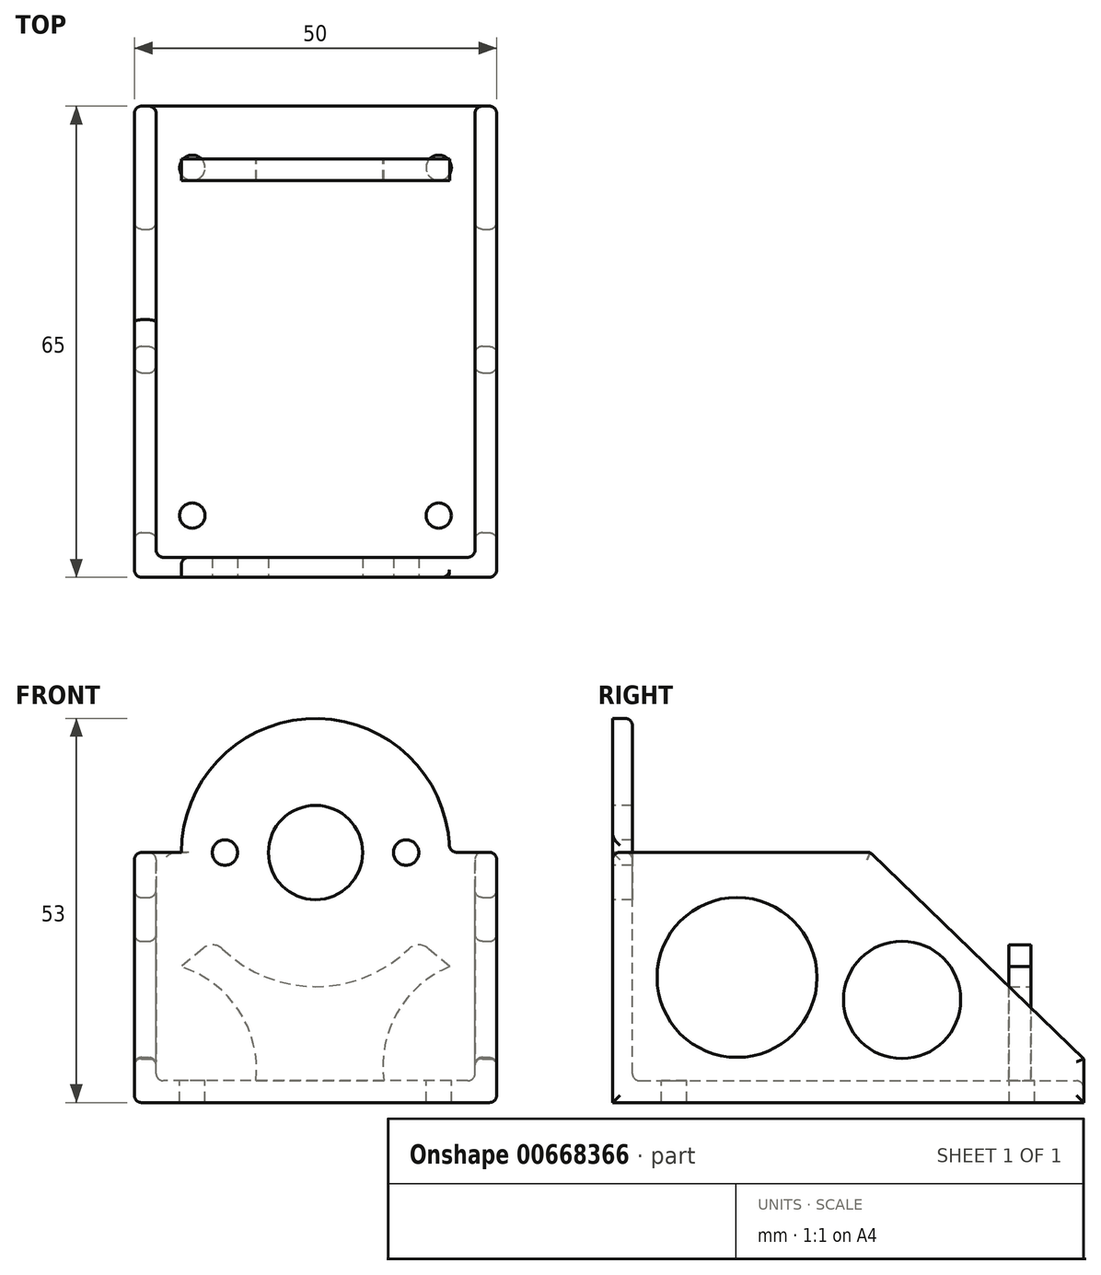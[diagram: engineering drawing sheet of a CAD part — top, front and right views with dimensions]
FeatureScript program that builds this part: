
annotation { "Feature Type Name" : "Feature", "Feature Type Description" : "" }
export const myFeature = defineFeature(function(context is Context, id is Id, definition is map)
    precondition{}
    {
        {
            var Q0;
            Q0=qCreatedBy(makeId("Top.planeOp"),FACE);
            var sketch = newSketch(context, id + "F0", { "sketchPlane" : qUnion([Q0])});
            skLineSegment(sketch, "E0.bottom", {"start": v(25, -32.5) * mm, "end": v(-25, -32.5) * mm});
            skLineSegment(sketch, "E0.top", {"start": v(25, 32.5) * mm, "end": v(-25, 32.5) * mm});
            skLineSegment(sketch, "E0.left", {"start": v(25, -32.5) * mm, "end": v(25, 32.5) * mm});
            skLineSegment(sketch, "E0.right", {"start": v(-25, -32.5) * mm, "end": v(-25, 32.5) * mm});
            skPoint(sketch, "E0.middle", {"position": v(0, 0) * mm});
            skSolve(sketch);
        }
        {
            var Q0;
            Q0 = qSketchRegion(id + "F0", true);
            extrude(context, id + "F1", {"entities" : qUnion([Q0]), "depth" : 53 * mm, "offsetDistance" : 25.4 * mm});
        }
        {
            var Q0;
            Q0=makeQuery(id+"F1.opExtrude","CAP_FACE",FACE,{"disambiguationData":[OSD([sQuery(id+"F0.wireOp",EDGE,"E0.bottom"),sQuery(id+"F0.wireOp",EDGE,"E0.top"),sQuery(id+"F0.wireOp",EDGE,"E0.left"),sQuery(id+"F0.wireOp",EDGE,"E0.right")])],"isStart":false});
            var sketch = newSketch(context, id + "F2", { "sketchPlane" : qUnion([Q0])});
            skLineSegment(sketch, "E1.bottom", {"start": v(22, -29.76) * mm, "end": v(-22, -29.76) * mm});
            skLineSegment(sketch, "E1.top", {"start": v(22, 34.24) * mm, "end": v(-22, 34.24) * mm});
            skLineSegment(sketch, "E1.left", {"start": v(22, -29.76) * mm, "end": v(22, 34.24) * mm});
            skLineSegment(sketch, "E1.right", {"start": v(-22, -29.76) * mm, "end": v(-22, 34.24) * mm});
            skPoint(sketch, "E1.middle", {"position": v(0, 2.24) * mm});
            skSolve(sketch);
        }
        {
            var Q0;
            Q0 = qSketchRegion(id + "F2", true);
            extrude(context, id + "F3", {"entities" : qUnion([Q0]), "operationType" : NewBodyOperationType.REMOVE, "oppositeDirection" : true, "depth" : 50 * mm, "offsetDistance" : 25.4 * mm});
        }
        {
            var Q0;
            Q0=makeQuery(id+"F1.opExtrude","SWEPT_FACE",FACE,{"disambiguationData":[OSD([sQuery(id+"F0.wireOp",EDGE,"E0.left")])]});
            var sketch = newSketch(context, id + "F4", { "sketchPlane" : qUnion([Q0])});
            skLineSegment(sketch, "E2", {"start": v(-16.13, 53) * mm, "end": v(32.5, 6.03) * mm});
            skSolve(sketch);
        }
        {
            var Q0;
            {var subQ0=sQuery(id+"F4.wireOp",EDGE,"E2");Q0=makeQuery(id+"F4.imprint","IMPRINT",FACE,{"disambiguationData":[TD([[makeQuery(id+"F4.imprint","IMPRINT",EDGE,{"derivedFrom":subQ0}),1.0]])]});}
            var Q1;
            Q1=sQuery(id+"F4.wireOp",EDGE,"E2");
            extrude(context, id + "F5", {"entities" : qUnion([Q0]), "operationType" : NewBodyOperationType.REMOVE, "surfaceEntities" : qUnion([Q1]), "oppositeDirection" : true, "depth" : 50.8 * mm, "offsetDistance" : 25.4 * mm});
        }
        {
            var Q0;
            Q0=makeQuery(id+"F1.opExtrude","SWEPT_FACE",FACE,{"disambiguationData":[OSD([sQuery(id+"F0.wireOp",EDGE,"E0.bottom")])]});
            var sketch = newSketch(context, id + "F6", { "sketchPlane" : qUnion([Q0])});
            skLineSegment(sketch, "E3", {"start": v(0, 0) * mm, "end": v(0, 34.5) * mm});
            skCircle(sketch, "E4", {"center": v(0, 34.5) * mm, "radius": 18.5 * mm});
            skLineSegment(sketch, "E5", {"start": v(0, 34.5) * mm, "end": v(12.5, 34.5) * mm});
            skLineSegment(sketch, "E6", {"start": v(12.5, 34.5) * mm, "end": v(0, 34.5) * mm});
            skLineSegment(sketch, "E7", {"start": v(0, 34.5) * mm, "end": v(-12.5, 34.5) * mm});
            skCircle(sketch, "E8", {"center": v(-12.5, 34.5) * mm, "radius": 1.75 * mm});
            skCircle(sketch, "E9", {"center": v(12.5, 34.5) * mm, "radius": 1.75 * mm});
            skCircle(sketch, "E10", {"center": v(0, 34.5) * mm, "radius": 6.5 * mm});
            skLineSegment(sketch, "E11", {"start": v(18.5, 34.53) * mm, "end": v(25, 34.53) * mm});
            skLineSegment(sketch, "E12", {"start": v(-18.5, 34.5) * mm, "end": v(-25, 34.5) * mm});
            skSolve(sketch);
        }
        {
            var Q0;
            Q0=makeQuery(id+"F6.imprint","IMPRINT",FACE,{"disambiguationData":[TD([[makeQuery(id+"F6.imprint","IMPRINT",EDGE,{"derivedFrom":sQuery(id+"F6.wireOp",EDGE,"E8")}),1.0]])]});
            var Q1;
            Q1=makeQuery(id+"F6.imprint","IMPRINT",FACE,{"disambiguationData":[TD([[makeQuery(id+"F6.imprint","IMPRINT",EDGE,{"derivedFrom":sQuery(id+"F6.wireOp",EDGE,"E9")}),1.0]])]});
            var Q2;
            {var subQ1=sQuery(id+"F6.wireOp",EDGE,"E6");var subQ3=sQuery(id+"F6.wireOp",EDGE,"E10");var subQ4=makeQuery(id+"F6.imprint","INTERSECT",VERTEX,{"derivedFrom":[subQ1,subQ3]});Q2=makeQuery(id+"F6.imprint","IMPRINT",FACE,{"disambiguationData":[TD([[makeQuery(id+"F6.imprint","IMPRINT",EDGE,{"disambiguationData":[TD([[subQ4,-1.0]])],"derivedFrom":subQ3}),1.0]])]});}
            var Q3;
            {var subQ1=sQuery(id+"F6.wireOp",EDGE,"E3");var subQ3=sQuery(id+"F6.wireOp",EDGE,"E10");var subQ4=makeQuery(id+"F6.imprint","INTERSECT",VERTEX,{"derivedFrom":[subQ1,subQ3]});Q3=makeQuery(id+"F6.imprint","IMPRINT",FACE,{"disambiguationData":[TD([[makeQuery(id+"F6.imprint","IMPRINT",EDGE,{"disambiguationData":[TD([[subQ4,-1.0]])],"derivedFrom":subQ3}),1.0]])]});}
            var Q4;
            {var subQ1=sQuery(id+"F6.wireOp",EDGE,"E3");var subQ3=sQuery(id+"F6.wireOp",EDGE,"E10");var subQ4=makeQuery(id+"F6.imprint","INTERSECT",VERTEX,{"derivedFrom":[subQ1,subQ3]});Q4=makeQuery(id+"F6.imprint","IMPRINT",FACE,{"disambiguationData":[TD([[makeQuery(id+"F6.imprint","IMPRINT",EDGE,{"disambiguationData":[TD([[subQ4,1.0]])],"derivedFrom":subQ3}),1.0]])]});}
            var Q5;
            {var subQ0=sQuery(id+"F6.wireOp",EDGE,"E12");Q5=makeQuery(id+"F6.imprint","IMPRINT",FACE,{"disambiguationData":[TD([[makeQuery(id+"F6.imprint","IMPRINT",EDGE,{"derivedFrom":subQ0}),-1.0]])]});}
            var Q6;
            {var subQ0=sQuery(id+"F6.wireOp",EDGE,"E11");Q6=makeQuery(id+"F6.imprint","IMPRINT",FACE,{"disambiguationData":[TD([[makeQuery(id+"F6.imprint","IMPRINT",EDGE,{"derivedFrom":subQ0}),1.0]])]});}
            extrude(context, id + "F7", {"entities" : qUnion([Q0, Q1, Q2, Q3, Q4, Q5, Q6]), "operationType" : NewBodyOperationType.REMOVE, "oppositeDirection" : true, "depth" : 46.48 * mm, "offsetDistance" : 25.4 * mm});
        }
        {
            var Q0;
            Q0=makeQuery(id+"F1.opExtrude","SWEPT_FACE",FACE,{"disambiguationData":[OSD([sQuery(id+"F0.wireOp",EDGE,"E0.left")])]});
            var sketch = newSketch(context, id + "F8", { "sketchPlane" : qUnion([Q0])});
            skCircle(sketch, "E13", {"center": v(-15.34, 17.27) * mm, "radius": 11.03 * mm});
            skPoint(sketch, "E13.centerSnap0", {"position": v(-32.5, 17.27) * mm});
            skLineSegment(sketch, "E14", {"start": v(-13.31, 6.42) * mm, "end": v(32.1, 6.42) * mm});
            skCircle(sketch, "E15", {"center": v(7.43, 14.17) * mm, "radius": 8.1 * mm});
            skSolve(sketch);
        }
        {
            var Q0;
            Q0 = qSketchRegion(id + "F8", true);
            extrude(context, id + "F9", {"entities" : qUnion([Q0]), "operationType" : NewBodyOperationType.REMOVE, "oppositeDirection" : true, "depth" : 51.05 * mm, "offsetDistance" : 25.4 * mm});
        }
        {
            var Q0;
            Q0=makeQuery(id+"F1.opExtrude","SWEPT_FACE",FACE,{"disambiguationData":[OSD([sQuery(id+"F0.wireOp",EDGE,"E0.left")])]});
            var Q1;
            Q1=makeQuery(id+"F3.boolean.opBoolean","COPY",FACE,{"derivedFrom":makeQuery(id+"F3.opExtrude","SWEPT_FACE",FACE,{"disambiguationData":[OSD([sQuery(id+"F2.wireOp",EDGE,"E1.right")])]})});
            var Q2;
            Q2=makeQuery(id+"F3.boolean.opBoolean","COPY",FACE,{"derivedFrom":makeQuery(id+"F3.opExtrude","SWEPT_FACE",FACE,{"disambiguationData":[OSD([sQuery(id+"F2.wireOp",EDGE,"E1.left")])]})});
            var Q3;
            Q3=makeQuery(id+"F1.opExtrude","SWEPT_FACE",FACE,{"disambiguationData":[OSD([sQuery(id+"F0.wireOp",EDGE,"E0.right")])]});
            var Q4;
            Q4=makeQuery(id+"F3.boolean.opBoolean","COPY",FACE,{"derivedFrom":makeQuery(id+"F3.opExtrude","CAP_FACE",FACE,{"disambiguationData":[OSD([sQuery(id+"F2.wireOp",EDGE,"E1.bottom"),sQuery(id+"F2.wireOp",EDGE,"E1.top"),sQuery(id+"F2.wireOp",EDGE,"E1.left"),sQuery(id+"F2.wireOp",EDGE,"E1.right")])],"isStart":false})});
            var Q5;
            {var subQ0=sQuery(id+"F6.wireOp",EDGE,"E4");Q5=makeQuery(id+"F7.boolean.opBoolean","INTERSECT",EDGE,{"derivedFrom":[makeQuery(id+"F3.boolean.opBoolean","COPY",FACE,{"derivedFrom":makeQuery(id+"F3.opExtrude","SWEPT_FACE",FACE,{"disambiguationData":[OSD([sQuery(id+"F2.wireOp",EDGE,"E1.bottom")])]})}),makeQuery(id+"F7.opExtrude","SWEPT_FACE",FACE,{"disambiguationData":[OSD([subQ0]),TDD([makeQuery(id+"F6.imprint","IMPRINT",EDGE,{"disambiguationData":[TD([[makeQuery(id+"F6.imprint","INTERSECT",VERTEX,{"derivedFrom":[subQ0,sQuery(id+"F6.wireOp",EDGE,"E11")]}),-1.0]])],"derivedFrom":subQ0})])]}),makeQuery(id+"F7.opExtrude","SWEPT_FACE",FACE,{"disambiguationData":[OSD([subQ0]),TDD([makeQuery(id+"F6.imprint","IMPRINT",EDGE,{"disambiguationData":[TD([[makeQuery(id+"F6.imprint","INTERSECT",VERTEX,{"derivedFrom":[subQ0,sQuery(id+"F6.wireOp",EDGE,"E12")]}),1.0]])],"derivedFrom":subQ0})])]})]});}
            var Q6;
            Q6=makeQuery(id+"F7.boolean.opBoolean","COPY",FACE,{"derivedFrom":makeQuery(id+"F7.opExtrude","SWEPT_FACE",FACE,{"disambiguationData":[OSD([sQuery(id+"F6.wireOp",EDGE,"E11")])]})});
            var Q7;
            {var subQ0=sQuery(id+"F6.wireOp",EDGE,"E4");Q7=makeQuery(id+"F7.boolean.opBoolean","TWEAK_FACE",FACE,{"derivedFrom":[makeQuery(id+"F7.opExtrude","SWEPT_FACE",FACE,{"disambiguationData":[OSD([subQ0]),TDD([makeQuery(id+"F6.imprint","IMPRINT",EDGE,{"disambiguationData":[TD([[makeQuery(id+"F6.imprint","INTERSECT",VERTEX,{"derivedFrom":[subQ0,sQuery(id+"F6.wireOp",EDGE,"E11")]}),-1.0]])],"derivedFrom":subQ0})])]}),makeQuery(id+"F7.opExtrude","SWEPT_FACE",FACE,{"disambiguationData":[OSD([subQ0]),TDD([makeQuery(id+"F6.imprint","IMPRINT",EDGE,{"disambiguationData":[TD([[makeQuery(id+"F6.imprint","INTERSECT",VERTEX,{"derivedFrom":[subQ0,sQuery(id+"F6.wireOp",EDGE,"E12")]}),1.0]])],"derivedFrom":subQ0})])]})]});}
            var Q8;
            Q8=makeQuery(id+"F7.boolean.opBoolean","COPY",EDGE,{"derivedFrom":makeQuery(id+"F7.opExtrude","CAP_EDGE",EDGE,{"disambiguationData":[OSD([sQuery(id+"F6.wireOp",EDGE,"E12")])],"isStart":true})});
            fillet(context, id + "F10", {"entities" : qUnion([Q0, Q1, Q2, Q3, Q4, Q5, Q6, Q7, Q8]), "radius" : 1 * mm, "tangentPropagation" : true, "allowEdgeOverflow" : false});
        }
        {
            var Q0;
            Q0=makeQuery(id+"F3.boolean.opBoolean","COPY",FACE,{"derivedFrom":makeQuery(id+"F3.opExtrude","CAP_FACE",FACE,{"disambiguationData":[OSD([sQuery(id+"F2.wireOp",EDGE,"E1.bottom"),sQuery(id+"F2.wireOp",EDGE,"E1.top"),sQuery(id+"F2.wireOp",EDGE,"E1.left"),sQuery(id+"F2.wireOp",EDGE,"E1.right")])],"isStart":false})});
            var sketch = newSketch(context, id + "F11", { "sketchPlane" : qUnion([Q0])});
            skLineSegment(sketch, "E16.bottom", {"start": v(-17, -24) * mm, "end": v(17, -24) * mm});
            skLineSegment(sketch, "E16.top", {"start": v(-17, 24) * mm, "end": v(17, 24) * mm});
            skLineSegment(sketch, "E16.left", {"start": v(-17, -24) * mm, "end": v(-17, 24) * mm});
            skLineSegment(sketch, "E16.right", {"start": v(17, -24) * mm, "end": v(17, 24) * mm});
            skPoint(sketch, "E16.middle", {"position": v(0, 0) * mm});
            skCircle(sketch, "E17", {"center": v(17, -24) * mm, "radius": 1.75 * mm});
            skCircle(sketch, "E18", {"center": v(-17, -24) * mm, "radius": 1.75 * mm});
            skCircle(sketch, "E19", {"center": v(17, 24) * mm, "radius": 1.75 * mm});
            skCircle(sketch, "E20", {"center": v(-17, 24) * mm, "radius": 1.75 * mm});
            skSolve(sketch);
        }
        {
            var Q0;
            {var subQ0=sQuery(id+"F11.wireOp",EDGE,"E16.left");var subQ1=sQuery(id+"F11.wireOp",EDGE,"E16.top");var subQ2=makeQuery(id+"F11.imprint","INTERSECT",VERTEX,{"derivedFrom":[subQ1,subQ0]});Q0=makeQuery(id+"F11.imprint","IMPRINT",FACE,{"disambiguationData":[TD([[makeQuery(id+"F11.imprint","IMPRINT",EDGE,{"disambiguationData":[TD([[subQ2,-1.0]])],"derivedFrom":subQ1}),1.0]])]});}
            var Q1;
            {var subQ0=sQuery(id+"F11.wireOp",EDGE,"E16.right");var subQ1=sQuery(id+"F11.wireOp",EDGE,"E16.top");var subQ2=makeQuery(id+"F11.imprint","INTERSECT",VERTEX,{"derivedFrom":[subQ1,subQ0]});Q1=makeQuery(id+"F11.imprint","IMPRINT",FACE,{"disambiguationData":[TD([[makeQuery(id+"F11.imprint","IMPRINT",EDGE,{"disambiguationData":[TD([[subQ2,1.0]])],"derivedFrom":subQ1}),1.0]])]});}
            var Q2;
            {var subQ0=sQuery(id+"F11.wireOp",EDGE,"E16.right");var subQ1=sQuery(id+"F11.wireOp",EDGE,"E16.top");var subQ2=makeQuery(id+"F11.imprint","INTERSECT",VERTEX,{"derivedFrom":[subQ1,subQ0]});Q2=makeQuery(id+"F11.imprint","IMPRINT",FACE,{"disambiguationData":[TD([[makeQuery(id+"F11.imprint","IMPRINT",EDGE,{"disambiguationData":[TD([[subQ2,1.0]])],"derivedFrom":subQ1}),-1.0]])]});}
            var Q3;
            {var subQ0=sQuery(id+"F11.wireOp",EDGE,"E16.left");var subQ1=sQuery(id+"F11.wireOp",EDGE,"E16.top");var subQ2=makeQuery(id+"F11.imprint","INTERSECT",VERTEX,{"derivedFrom":[subQ1,subQ0]});Q3=makeQuery(id+"F11.imprint","IMPRINT",FACE,{"disambiguationData":[TD([[makeQuery(id+"F11.imprint","IMPRINT",EDGE,{"disambiguationData":[TD([[subQ2,-1.0]])],"derivedFrom":subQ1}),-1.0]])]});}
            var Q4;
            {var subQ0=sQuery(id+"F11.wireOp",EDGE,"E16.right");var subQ1=sQuery(id+"F11.wireOp",EDGE,"E16.bottom");var subQ2=makeQuery(id+"F11.imprint","INTERSECT",VERTEX,{"derivedFrom":[subQ1,subQ0]});Q4=makeQuery(id+"F11.imprint","IMPRINT",FACE,{"disambiguationData":[TD([[makeQuery(id+"F11.imprint","IMPRINT",EDGE,{"disambiguationData":[TD([[subQ2,1.0]])],"derivedFrom":subQ1}),-1.0]])]});}
            var Q5;
            {var subQ0=sQuery(id+"F11.wireOp",EDGE,"E16.left");var subQ1=sQuery(id+"F11.wireOp",EDGE,"E16.bottom");var subQ2=makeQuery(id+"F11.imprint","INTERSECT",VERTEX,{"derivedFrom":[subQ1,subQ0]});Q5=makeQuery(id+"F11.imprint","IMPRINT",FACE,{"disambiguationData":[TD([[makeQuery(id+"F11.imprint","IMPRINT",EDGE,{"disambiguationData":[TD([[subQ2,-1.0]])],"derivedFrom":subQ1}),-1.0]])]});}
            var Q6;
            {var subQ0=sQuery(id+"F11.wireOp",EDGE,"E16.right");var subQ1=sQuery(id+"F11.wireOp",EDGE,"E16.bottom");var subQ2=makeQuery(id+"F11.imprint","INTERSECT",VERTEX,{"derivedFrom":[subQ1,subQ0]});Q6=makeQuery(id+"F11.imprint","IMPRINT",FACE,{"disambiguationData":[TD([[makeQuery(id+"F11.imprint","IMPRINT",EDGE,{"disambiguationData":[TD([[subQ2,1.0]])],"derivedFrom":subQ1}),1.0]])]});}
            var Q7;
            {var subQ0=sQuery(id+"F11.wireOp",EDGE,"E16.left");var subQ1=sQuery(id+"F11.wireOp",EDGE,"E16.bottom");var subQ2=makeQuery(id+"F11.imprint","INTERSECT",VERTEX,{"derivedFrom":[subQ1,subQ0]});Q7=makeQuery(id+"F11.imprint","IMPRINT",FACE,{"disambiguationData":[TD([[makeQuery(id+"F11.imprint","IMPRINT",EDGE,{"disambiguationData":[TD([[subQ2,-1.0]])],"derivedFrom":subQ1}),1.0]])]});}
            extrude(context, id + "F12", {"entities" : qUnion([Q0, Q1, Q2, Q3, Q4, Q5, Q6, Q7]), "operationType" : NewBodyOperationType.REMOVE, "oppositeDirection" : true, "depth" : 25.4 * mm, "offsetDistance" : 25.4 * mm});
        }
        {
            var Q0;
            Q0=makeQuery(id+"F3.boolean.opBoolean","COPY",FACE,{"derivedFrom":makeQuery(id+"F3.opExtrude","CAP_FACE",FACE,{"disambiguationData":[OSD([sQuery(id+"F2.wireOp",EDGE,"E1.bottom"),sQuery(id+"F2.wireOp",EDGE,"E1.top"),sQuery(id+"F2.wireOp",EDGE,"E1.left"),sQuery(id+"F2.wireOp",EDGE,"E1.right")])],"isStart":false})});
            var sketch = newSketch(context, id + "F13", { "sketchPlane" : qUnion([Q0])});
            skLineSegment(sketch, "E21", {"start": v(0, 8.7) * mm, "end": v(0, 23.7) * mm});
            skLineSegment(sketch, "E22.bottom", {"start": v(-18.5, 22.2) * mm, "end": v(18.5, 22.2) * mm});
            skLineSegment(sketch, "E22.top", {"start": v(-18.5, 25.2) * mm, "end": v(18.5, 25.2) * mm});
            skLineSegment(sketch, "E22.left", {"start": v(-18.5, 22.2) * mm, "end": v(-18.5, 25.2) * mm});
            skLineSegment(sketch, "E22.right", {"start": v(18.5, 22.2) * mm, "end": v(18.5, 25.2) * mm});
            skPoint(sketch, "E22.middle", {"position": v(0, 23.7) * mm});
            skSolve(sketch);
        }
        {
            var Q0;
            Q0 = qSketchRegion(id + "F13", true);
            extrude(context, id + "F14", {"entities" : qUnion([Q0]), "operationType" : NewBodyOperationType.ADD, "depth" : 31.5 * mm, "offsetDistance" : 25.4 * mm});
        }
        {
            var Q0;
            Q0=makeQuery(id+"F14.opExtrude","SWEPT_FACE",FACE,{"disambiguationData":[OSD([sQuery(id+"F13.wireOp",EDGE,"E22.top")])]});
            var sketch = newSketch(context, id + "F15", { "sketchPlane" : qUnion([Q0])});
            skCircle(sketch, "E23", {"center": v(0, 34.5) * mm, "radius": 18.5 * mm});
            skArc(sketch, "E24", {"start": v(-9.44, 3) * mm, "mid": v(-11.27, 12.43) * mm, "end": v(-18.5, 18.75) * mm});
            skArc(sketch, "E25", {"start": v(18.5, 18.75) * mm, "mid": v(10.58, 12.69) * mm, "end": v(8.2, 3) * mm});
            skLineSegment(sketch, "E26", {"start": v(-18.5, 18.75) * mm, "end": v(0, 34.5) * mm});
            skLineSegment(sketch, "E27", {"start": v(0, 34.5) * mm, "end": v(18.5, 18.75) * mm});
            skSolve(sketch);
        }
        {
            var Q0;
            {var subQ1=sQuery(id+"F13.wireOp",EDGE,"E22.top");var subQ2=makeQuery(id+"F14.opExtrude","CAP_EDGE",EDGE,{"disambiguationData":[OSD([subQ1])],"isStart":false});Q0=makeQuery(id+"F15.imprint","IMPRINT",FACE,{"disambiguationData":[TD([[makeQuery(id+"F15.imprint","IMPRINT",EDGE,{"derivedFrom":subQ2}),1.0]])]});}
            var Q1;
            {var subQ0=sQuery(id+"F15.wireOp",EDGE,"E24");Q1=makeQuery(id+"F15.imprint","IMPRINT",FACE,{"disambiguationData":[TD([[makeQuery(id+"F15.imprint","IMPRINT",EDGE,{"derivedFrom":subQ0}),1.0]])]});}
            var Q2;
            {var subQ0=sQuery(id+"F15.wireOp",EDGE,"E25");Q2=makeQuery(id+"F15.imprint","IMPRINT",FACE,{"disambiguationData":[TD([[makeQuery(id+"F15.imprint","IMPRINT",EDGE,{"derivedFrom":subQ0}),1.0]])]});}
            var Q3;
            {var subQ0=sQuery(id+"F15.wireOp",EDGE,"E26");var subQ1=sQuery(id+"F15.wireOp",EDGE,"E23");var subQ2=makeQuery(id+"F15.imprint","INTERSECT",VERTEX,{"derivedFrom":[subQ1,subQ0]});Q3=makeQuery(id+"F15.imprint","IMPRINT",FACE,{"disambiguationData":[TD([[makeQuery(id+"F15.imprint","IMPRINT",EDGE,{"disambiguationData":[TD([[subQ2,-1.0]])],"derivedFrom":subQ1}),1.0]])]});}
            var Q4;
            {var subQ0=sQuery(id+"F15.wireOp",EDGE,"E23");var subQ4=sQuery(id+"F15.wireOp",EDGE,"E27");var subQ5=makeQuery(id+"F15.imprint","INTERSECT",VERTEX,{"derivedFrom":[subQ0,subQ4]});Q4=makeQuery(id+"F15.imprint","IMPRINT",FACE,{"disambiguationData":[TD([[makeQuery(id+"F15.imprint","IMPRINT",EDGE,{"disambiguationData":[TD([[subQ5,-1.0]])],"derivedFrom":subQ0}),-1.0]])]});}
            var Q5;
            {var subQ0=sQuery(id+"F15.wireOp",EDGE,"E23");var subQ4=sQuery(id+"F15.wireOp",EDGE,"E26");var subQ5=makeQuery(id+"F15.imprint","INTERSECT",VERTEX,{"derivedFrom":[subQ0,subQ4]});Q5=makeQuery(id+"F15.imprint","IMPRINT",FACE,{"disambiguationData":[TD([[makeQuery(id+"F15.imprint","IMPRINT",EDGE,{"disambiguationData":[TD([[subQ5,1.0]])],"derivedFrom":subQ0}),-1.0]])]});}
            extrude(context, id + "F16", {"entities" : qUnion([Q0, Q1, Q2, Q3, Q4, Q5]), "operationType" : NewBodyOperationType.REMOVE, "oppositeDirection" : true, "depth" : 25.4 * mm, "offsetDistance" : 25.4 * mm});
        }
        {
            var Q0;
            Q0=makeQuery(id+"F16.boolean.opBoolean","COPY",EDGE,{"derivedFrom":makeQuery(id+"F16.opExtrude","SWEPT_EDGE",EDGE,{"disambiguationData":[OSD([sQuery(id+"F15.wireOp",EDGE,"E23"),sQuery(id+"F15.wireOp",EDGE,"E26")])]})});
            var Q1;
            Q1=makeQuery(id+"F16.boolean.opBoolean","COPY",EDGE,{"derivedFrom":makeQuery(id+"F16.opExtrude","SWEPT_EDGE",EDGE,{"disambiguationData":[OSD([sQuery(id+"F15.wireOp",EDGE,"E23"),sQuery(id+"F15.wireOp",EDGE,"E27")])]})});
            var Q2;
            {var subQ0=sQuery(id+"F15.wireOp",EDGE,"E27");var subQ1=sQuery(id+"F15.wireOp",EDGE,"E25");var subQ2=sQuery(id+"F13.wireOp",EDGE,"E22.left");var subQ3=sQuery(id+"F13.wireOp",EDGE,"E22.top");Q2=makeQuery(id+"F16.boolean.opBoolean","TWEAK_EDGE",EDGE,{"derivedFrom":[makeQuery(id+"F16.opExtrude","SWEPT_EDGE",EDGE,{"disambiguationData":[OSD([subQ3,subQ2,subQ1,subQ0]),OD(0.0)]}),makeQuery(id+"F16.opExtrude","SWEPT_EDGE",EDGE,{"disambiguationData":[OSD([subQ3,subQ2,subQ1,subQ0]),OD(1.0)]})]});}
            var Q3;
            {var subQ0=sQuery(id+"F15.wireOp",EDGE,"E26");var subQ1=sQuery(id+"F15.wireOp",EDGE,"E24");var subQ2=sQuery(id+"F13.wireOp",EDGE,"E22.right");var subQ3=sQuery(id+"F13.wireOp",EDGE,"E22.top");Q3=makeQuery(id+"F16.boolean.opBoolean","TWEAK_EDGE",EDGE,{"derivedFrom":[makeQuery(id+"F16.opExtrude","SWEPT_EDGE",EDGE,{"disambiguationData":[OSD([subQ3,subQ2,subQ1,subQ0]),OD(0.0)]}),makeQuery(id+"F16.opExtrude","SWEPT_EDGE",EDGE,{"disambiguationData":[OSD([subQ3,subQ2,subQ1,subQ0]),OD(1.0)]})]});}
            var Q4;
            Q4=makeQuery(id+"F16.boolean.opBoolean","COPY",EDGE,{"derivedFrom":makeQuery(id+"F16.opExtrude","SWEPT_EDGE",EDGE,{"disambiguationData":[OSD([sQuery(id+"F13.wireOp",EDGE,"E22.top"),sQuery(id+"F15.wireOp",EDGE,"E24")])]})});
            var Q5;
            Q5=makeQuery(id+"F14.opExtrude","CAP_EDGE",EDGE,{"disambiguationData":[OSD([sQuery(id+"F13.wireOp",EDGE,"E22.top")])],"isStart":true});
            var Q6;
            Q6=makeQuery(id+"F16.boolean.opBoolean","COPY",EDGE,{"derivedFrom":makeQuery(id+"F16.opExtrude","SWEPT_EDGE",EDGE,{"disambiguationData":[OSD([sQuery(id+"F13.wireOp",EDGE,"E22.top"),sQuery(id+"F15.wireOp",EDGE,"E25")])]})});
            var Q7;
            Q7=makeQuery(id+"F14.opExtrude","CAP_EDGE",EDGE,{"disambiguationData":[OSD([sQuery(id+"F13.wireOp",EDGE,"E22.bottom")])],"isStart":true});
            fillet(context, id + "F17", {"entities" : qUnion([Q0, Q1, Q2, Q3, Q4, Q5, Q6, Q7]), "radius" : 2 * mm, "tangentPropagation" : true, "allowEdgeOverflow" : false});
        }
    });
